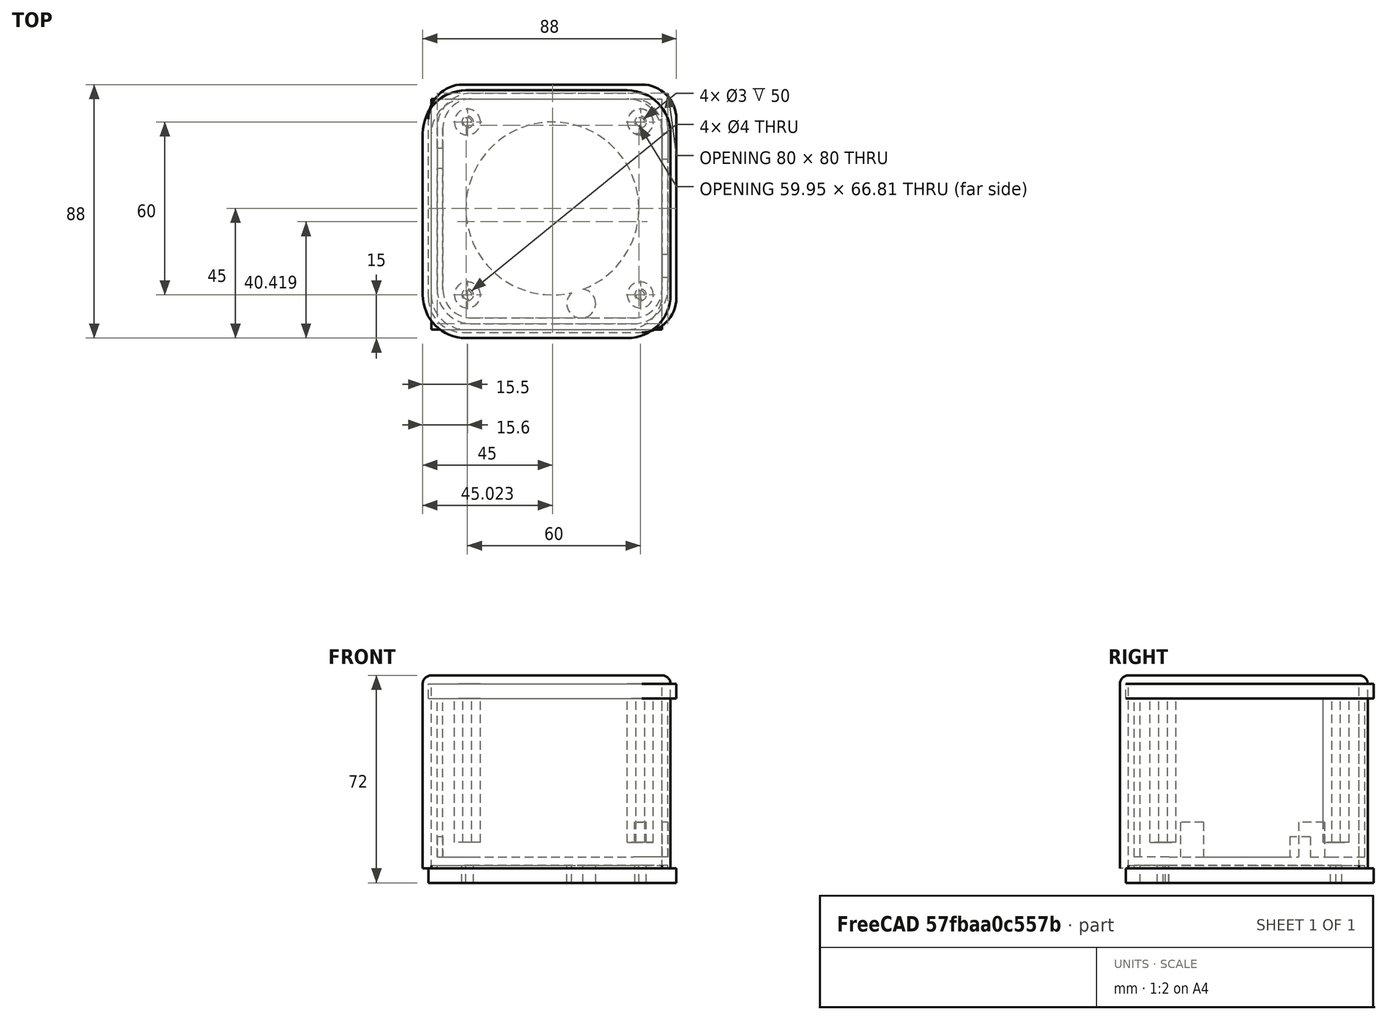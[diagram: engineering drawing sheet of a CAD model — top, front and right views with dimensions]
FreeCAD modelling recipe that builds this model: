
FCSTD DOCUMENT  (FreeCAD 0.17R13522 (Git))
Label: JoselitoBOX_V2_1
License: All rights reserved
LicenseURL: http://en.wikipedia.org/wiki/All_rights_reserved
objects: Part::Cylinder×12, Part::Box×9, Part::Cut×6, Part::MultiFuse×6, Part::Fillet×5, Part::Thickness×2
note: 40 computed .brp shape members not serialized (recipe doc carries the construction recipe); baked Part::Feature solids carry a one-line shape summary decoded from their .brp

FEATURE [Part::Box] Box002  label="Cubo002"
  AttacherType = Attacher::AttachEngine3D
  Height = 1
  Length = 80
  Width = 80
FEATURE [Part::Box] Box001  label="Cubo001"
  AttacherType = Attacher::AttachEngine3D
  Height = 64
  Length = 80
  Width = 80
FEATURE [Part::Fillet] Fillet
  Base = -> Box001
  Edges = 4 edges r=12: [Edge1,Edge3,Edge5,Edge7]
FEATURE [Part::Thickness] Thickness
  Faces = -> Fillet [Face5]
  Intersection = false
  Join = 0
  Mode = 0
  SelfIntersection = false
  Value = 3
FEATURE [Part::Box] Box  label="Cubo"
  AttacherType = Attacher::AttachEngine3D
  Height = 60
  Length = 80
  Width = 80
FEATURE [Part::Fillet] Fillet001
  Base = -> Box
  Edges = 4 edges r=12: [Edge1,Edge3,Edge5,Edge7]
FEATURE [Part::Thickness] Thickness001  label="CAJA"
  Faces = -> Fillet001 [Face5]
  Intersection = false
  Join = 0
  Mode = 0
  Placement = pos=(2,2,4) rot=(0,0,1;0rad)
  SelfIntersection = false
  Value = -2
FEATURE [Part::Cut] Cut001
  Placement = pos=(5.5,5,6) rot=(0,0,1;0rad)
FEATURE [Part::Cylinder] Cylinder002  label="Cilindro002"
  Angle = 360
  AttacherType = Attacher::AttachEngine3D
  Height = 63
  Placement = pos=(7,7,3) rot=(0,0,1;0rad)
  Radius = 1.5
FEATURE [Part::Cylinder] Cylinder003  label="Cilindro003"
  Angle = 360
  AttacherType = Attacher::AttachEngine3D
  Height = 55
  Placement = pos=(7,7,3) rot=(0,0,1;0rad)
  Radius = 4.5
FEATURE [Part::Cut] Cut002
  Base = -> Cylinder003
  Placement = pos=(5.5,65,6) rot=(0,0,1;0rad)
  Tool = -> Cylinder002
FEATURE [Part::Cylinder] Cylinder004  label="Cilindro004"
  Angle = 360
  AttacherType = Attacher::AttachEngine3D
  Height = 63
  Placement = pos=(7,7,3) rot=(0,0,1;0rad)
  Radius = 1.5
FEATURE [Part::Cylinder] Cylinder005  label="Cilindro005"
  Angle = 360
  AttacherType = Attacher::AttachEngine3D
  Height = 55
  Placement = pos=(7,7,3) rot=(0,0,1;0rad)
  Radius = 4.5
FEATURE [Part::Cut] Cut003
  Base = -> Cylinder005
  Placement = pos=(65.5,65,6) rot=(0,0,1;0rad)
  Tool = -> Cylinder004
FEATURE [Part::Cylinder] Cylinder006  label="Cilindro006"
  Angle = 360
  AttacherType = Attacher::AttachEngine3D
  Height = 63
  Placement = pos=(7,7,3) rot=(0,0,1;0rad)
  Radius = 1.5
FEATURE [Part::Cylinder] Cylinder007  label="Cilindro007"
  Angle = 360
  AttacherType = Attacher::AttachEngine3D
  Height = 55
  Placement = pos=(7,7,3) rot=(0,0,1;0rad)
  Radius = 4.5
FEATURE [Part::Cut] Cut004
  Base = -> Cylinder007
  Placement = pos=(65.5,5,6) rot=(0,0,1;0rad)
  Tool = -> Cylinder006
FEATURE [Part::MultiFuse] Fusion  label="cilindros"
  Shapes = -> [Cut001,Cut003,Cut004,Cut002]
FEATURE [Part::Box] Box003  label="Cubo003"
  AttacherType = Attacher::AttachEngine3D
  Height = 1
  Length = 80
  Width = 80
FEATURE [Part::Fillet] Fillet002
  Base = -> Box003
  Edges = 4 edges r=12: [Edge1,Edge3,Edge5,Edge7]
FEATURE [Part::Box] Box004  label="Cubo004"
  AttacherType = Attacher::AttachEngine3D
  Height = 5
  Length = 86
  Width = 86
FEATURE [Part::Fillet] Fillet003
  Base = -> Box004
  Edges = 4 edges r=12: [Edge1,Edge3,Edge5,Edge7]
  Placement = pos=(-3,-3,-5) rot=(0,0,1;0rad)
FEATURE [Part::Cylinder] Cylinder008  label="Speaker"
  Angle = 360
  AttacherType = Attacher::AttachEngine3D
  Height = 10
  Placement = pos=(42,42,-6) rot=(0,0,1;0rad)
  Radius = 30
FEATURE [Part::Cylinder] Cylinder009  label="LED"
  Angle = 360
  AttacherType = Attacher::AttachEngine3D
  Height = 10
  Placement = pos=(52,9,-6) rot=(0,0,1;0rad)
  Radius = 5
FEATURE [Part::MultiFuse] Fusion001  label="Tapa"
  Placement = pos=(2,2,0) rot=(0,0,1;0rad)
  Shapes = -> [Fillet002,Fillet003]
FEATURE [Part::Cylinder] Cylinder011  label="rod1"
  Angle = 360
  AttacherType = Attacher::AttachEngine3D
  Height = 63
  Placement = pos=(72.6,12,-9) rot=(0,0,1;0rad)
  Radius = 2
FEATURE [Part::Cylinder] Cylinder012  label="rod2"
  Angle = 360
  AttacherType = Attacher::AttachEngine3D
  Height = 63
  Placement = pos=(72.6,72,-9) rot=(0,0,1;0rad)
  Radius = 2
FEATURE [Part::Cylinder] Cylinder013  label="rod3"
  Angle = 360
  AttacherType = Attacher::AttachEngine3D
  Height = 63
  Placement = pos=(12.6,12,-9) rot=(0,0,1;0rad)
  Radius = 2
FEATURE [Part::Cylinder] Cylinder014  label="rod4"
  Angle = 360
  AttacherType = Attacher::AttachEngine3D
  Height = 63
  Placement = pos=(12.6,72,-9) rot=(0,0,1;0rad)
  Radius = 2
FEATURE [Part::Box] Box009  label="interruptor002"
  AttacherType = Attacher::AttachEngine3D
  Height = 17
  Length = 26
  Placement = pos=(62,20,-6) rot=(0,0,1;0rad)
  Width = 7
FEATURE [Part::Box] Box010  label="jackDC"
  AttacherType = Attacher::AttachEngine3D
  Height = 12
  Length = 26
  Placement = pos=(-4,15,4) rot=(0,0,1;0rad)
  Width = 9
FEATURE [Part::Box] Box011  label="jackAudio"
  AttacherType = Attacher::AttachEngine3D
  Height = 12
  Length = 26
  Placement = pos=(-4,57,4) rot=(0,0,1;0rad)
  Width = 8
FEATURE [Part::MultiFuse] Fusion002
  Placement = pos=(82,83,0) rot=(0,0,1;3.14159rad)
  Shapes = -> [Box009,Box010,Box011]
FEATURE [Part::MultiFuse] Fusion003  label="holes"
  Shapes = -> [Cylinder011,Cylinder009,Cylinder008,Cylinder012,Cylinder013,Cylinder014]
FEATURE [Part::Cut] Cut005  label="frontspeaker"
  Base = -> Fusion001
  Tool = -> Fusion003
FEATURE [Part::Box] Box012  label="Cubo005"
  AttacherType = Attacher::AttachEngine3D
  Height = 5
  Length = 86
  Width = 86
FEATURE [Part::Fillet] Fillet004
  Base = -> Box012
  Edges = 4 edges r=12: [Edge1,Edge3,Edge5,Edge7]
  Placement = pos=(-1,-1,59) rot=(0,0,1;0rad)
FEATURE [Part::MultiFuse] Fusion004
  Shapes = -> [Fusion,Thickness001]
FEATURE [Part::MultiFuse] Fusion005
  Shapes = -> [Fusion004,Fillet004]
FEATURE [Part::Cut] Cut  label="BOX_bases_holes"
  Base = -> Fusion005
  Tool = -> Fusion002
